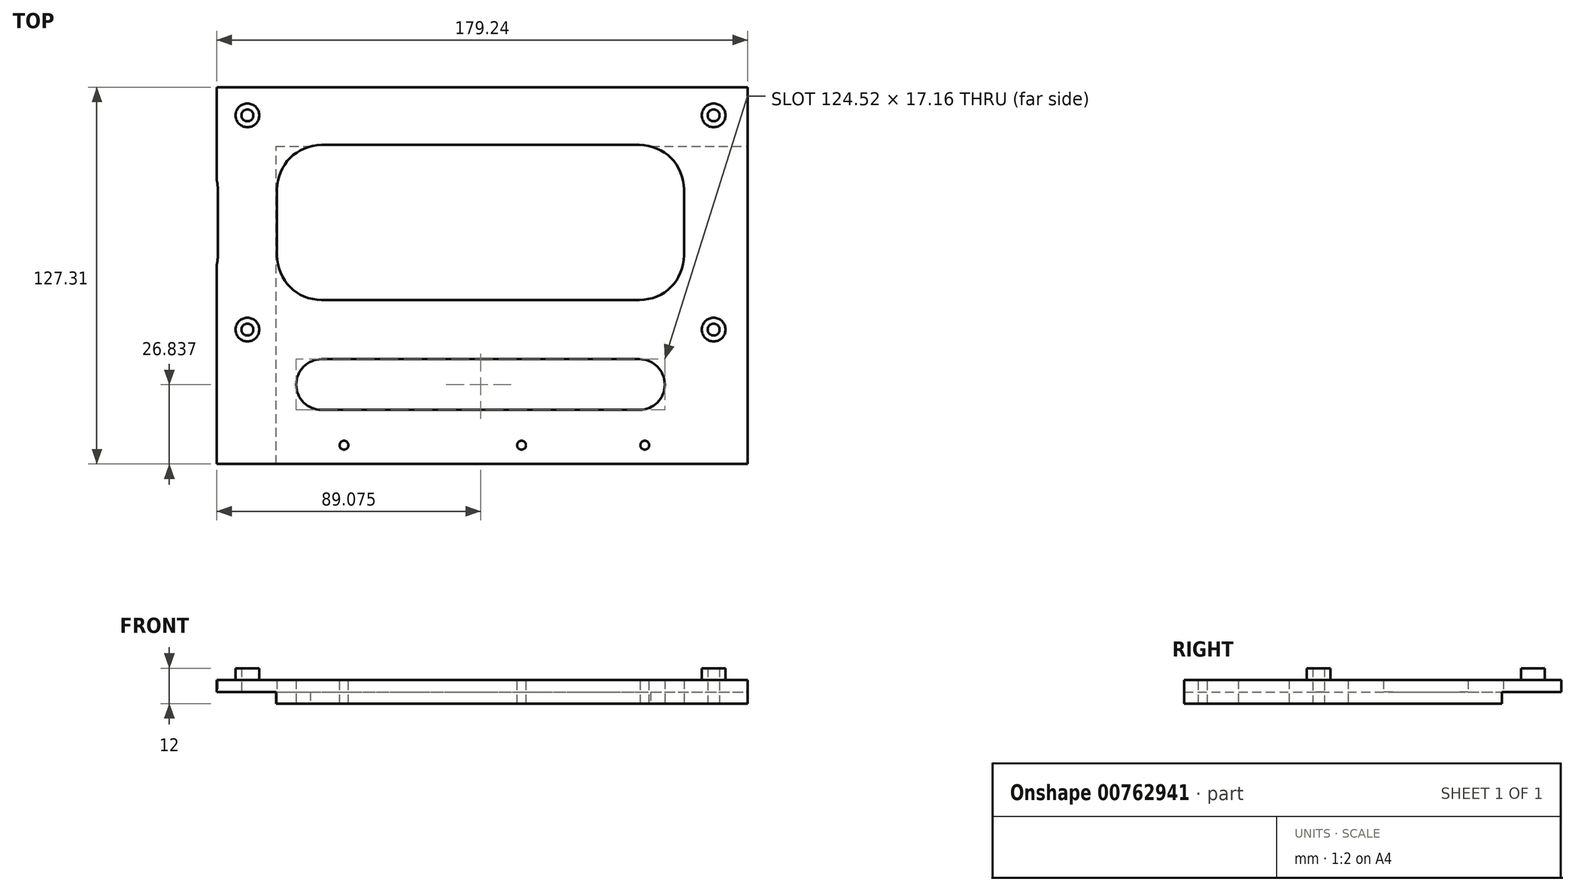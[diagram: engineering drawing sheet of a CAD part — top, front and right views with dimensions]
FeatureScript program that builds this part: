
annotation { "Feature Type Name" : "Feature", "Feature Type Description" : "" }
export const myFeature = defineFeature(function(context is Context, id is Id, definition is map)
    precondition{}
    {
        {
            var Q0;
            Q0=qCreatedBy(makeId("Top.planeOp"),FACE);
            var sketch = newSketch(context, id + "F0", { "sketchPlane" : qUnion([Q0])});
            skLineSegment(sketch, "E0.bottom", {"start": v(-84.85, 211.43) * mm, "end": v(248.95, 211.43) * mm});
            skLineSegment(sketch, "E0.left", {"start": v(-84.85, 211.43) * mm, "end": v(-84.85, -69.57) * mm});
            skLineSegment(sketch, "E0.right", {"start": v(248.95, 211.43) * mm, "end": v(248.95, -32.4) * mm});
            skCircle(sketch, "E1", {"center": v(-44.42, 203.18) * mm, "radius": 2 * mm});
            skCircle(sketch, "E2", {"center": v(-44.42, 48.24) * mm, "radius": 2 * mm});
            skCircle(sketch, "E3", {"center": v(-44.42, -24.15) * mm, "radius": 2 * mm});
            skCircle(sketch, "E4", {"center": v(80.04, -24.15) * mm, "radius": 2 * mm});
            skCircle(sketch, "E5", {"center": v(80.04, 48.24) * mm, "radius": 2 * mm});
            skCircle(sketch, "E6", {"center": v(80.04, 203.18) * mm, "radius": 2 * mm});
            skCircle(sketch, "E7", {"center": v(237.52, 48.24) * mm, "radius": 2 * mm});
            skCircle(sketch, "E8", {"center": v(237.52, -24.15) * mm, "radius": 2 * mm});
            skCircle(sketch, "E9", {"center": v(237.52, 180.32) * mm, "radius": 2 * mm});
            skLineSegment(sketch, "E10.left", {"start": v(-34.42, 178.12) * mm, "end": v(-34.42, 73.3) * mm});
            skLineSegment(sketch, "E10.right", {"start": v(70.04, 178.12) * mm, "end": v(70.04, 73.3) * mm});
            skLineSegment(sketch, "E11.bottom", {"start": v(-19.36, 58.24) * mm, "end": v(54.99, 58.24) * mm});
            skLineSegment(sketch, "E11.top", {"start": v(-19.36, 38.24) * mm, "end": v(54.99, 38.24) * mm});
            skLineSegment(sketch, "E12.left", {"start": v(-34.42, 23.18) * mm, "end": v(-34.42, 0.9) * mm});
            skLineSegment(sketch, "E12.right", {"start": v(70.04, 23.18) * mm, "end": v(70.04, 0.9) * mm});
            skLineSegment(sketch, "E13.left", {"start": v(90.04, 23.18) * mm, "end": v(90.04, 0.9) * mm});
            skLineSegment(sketch, "E13.right", {"start": v(227.52, 23.18) * mm, "end": v(227.52, 0.9) * mm});
            skLineSegment(sketch, "E14.bottom", {"start": v(212.47, -14.15) * mm, "end": v(105.1, -14.15) * mm});
            skLineSegment(sketch, "E14.top", {"start": v(212.47, 38.24) * mm, "end": v(105.1, 38.24) * mm});
            skLineSegment(sketch, "E15.bottom", {"start": v(212.47, 58.24) * mm, "end": v(105.1, 58.24) * mm});
            skLineSegment(sketch, "E15.top", {"start": v(212.47, 193.18) * mm, "end": v(105.1, 193.18) * mm});
            skLineSegment(sketch, "E16.left", {"start": v(90.04, 178.12) * mm, "end": v(90.04, 73.3) * mm});
            skLineSegment(sketch, "E17", {"start": v(-19.36, -14.15) * mm, "end": v(54.99, -14.15) * mm});
            skLineSegment(sketch, "E18", {"start": v(-19.36, 193.18) * mm, "end": v(54.99, 193.18) * mm});
            skLineSegment(sketch, "E19", {"start": v(212.47, 170.32) * mm, "end": v(212.47, 193.18) * mm});
            skLineSegment(sketch, "E20", {"start": v(227.52, 155.26) * mm, "end": v(227.52, 73.3) * mm});
            skLineSegment(sketch, "E21", {"start": v(54.99, -34.15) * mm, "end": v(-19.36, -34.15) * mm});
            skLineSegment(sketch, "E22.MirrorCS", {"start": v(212.47, -51.31) * mm, "end": v(105.1, -51.31) * mm});
            skLineSegment(sketch, "E23.MirrorCS", {"start": v(212.47, -34.15) * mm, "end": v(105.1, -34.15) * mm});
            skLineSegment(sketch, "E24.MirrorCS", {"start": v(-19.36, -51.31) * mm, "end": v(54.99, -51.31) * mm});
            skLineSegment(sketch, "E25", {"start": v(-84.85, -69.57) * mm, "end": v(248.95, -69.57) * mm});
            skLineSegment(sketch, "E26", {"start": v(248.95, -32.4) * mm, "end": v(248.95, -69.57) * mm});
            skLineSegment(sketch, "E27", {"start": v(-54.42, -42.73) * mm, "end": v(-54.42, 33.18) * mm});
            skLineSegment(sketch, "E28", {"start": v(-66.28, 33.18) * mm, "end": v(-66.28, -42.73) * mm});
            skArc(sketch, "E29", {"start": v(-54.42, 33.18) * mm, "mid": v(-60.35, 39.1) * mm, "end": v(-66.28, 33.18) * mm});
            skArc(sketch, "E30", {"start": v(-66.28, -42.73) * mm, "mid": v(-60.35, -48.66) * mm, "end": v(-54.42, -42.73) * mm});
            skArc(sketch, "E31", {"start": v(-34.42, 0.9) * mm, "mid": v(-30, -9.74) * mm, "end": v(-19.36, -14.15) * mm});
            skArc(sketch, "E32", {"start": v(-19.36, 38.24) * mm, "mid": v(-30, 33.83) * mm, "end": v(-34.42, 23.18) * mm});
            skArc(sketch, "E33", {"start": v(70.04, 23.18) * mm, "mid": v(65.63, 33.83) * mm, "end": v(54.99, 38.24) * mm});
            skArc(sketch, "E34", {"start": v(54.99, -14.15) * mm, "mid": v(65.63, -9.74) * mm, "end": v(70.04, 0.9) * mm});
            skArc(sketch, "E35", {"start": v(-19.36, -34.15) * mm, "mid": v(-27.94, -42.73) * mm, "end": v(-19.36, -51.31) * mm});
            skArc(sketch, "E36", {"start": v(54.99, -51.31) * mm, "mid": v(63.56, -42.73) * mm, "end": v(54.99, -34.15) * mm});
            skArc(sketch, "E37", {"start": v(105.1, -34.15) * mm, "mid": v(96.52, -42.73) * mm, "end": v(105.1, -51.31) * mm});
            skArc(sketch, "E38", {"start": v(212.47, -51.31) * mm, "mid": v(221.04, -42.73) * mm, "end": v(212.47, -34.15) * mm});
            skArc(sketch, "E39", {"start": v(212.47, -14.15) * mm, "mid": v(223.11, -9.74) * mm, "end": v(227.52, 0.9) * mm});
            skArc(sketch, "E40", {"start": v(227.52, 23.18) * mm, "mid": v(223.11, 33.83) * mm, "end": v(212.47, 38.24) * mm});
            skArc(sketch, "E41", {"start": v(105.1, 38.24) * mm, "mid": v(94.46, 33.83) * mm, "end": v(90.04, 23.18) * mm});
            skArc(sketch, "E42", {"start": v(90.04, 0.9) * mm, "mid": v(94.46, -9.74) * mm, "end": v(105.1, -14.15) * mm});
            skArc(sketch, "E43", {"start": v(105.1, 193.18) * mm, "mid": v(94.46, 188.77) * mm, "end": v(90.04, 178.12) * mm});
            skArc(sketch, "E44", {"start": v(70.04, 178.12) * mm, "mid": v(65.63, 188.77) * mm, "end": v(54.99, 193.18) * mm});
            skArc(sketch, "E45", {"start": v(-19.36, 193.18) * mm, "mid": v(-30, 188.77) * mm, "end": v(-34.42, 178.12) * mm});
            skArc(sketch, "E46", {"start": v(-34.42, 73.3) * mm, "mid": v(-30, 62.65) * mm, "end": v(-19.36, 58.24) * mm});
            skArc(sketch, "E47", {"start": v(54.99, 58.24) * mm, "mid": v(65.63, 62.65) * mm, "end": v(70.04, 73.3) * mm});
            skArc(sketch, "E48", {"start": v(90.04, 73.3) * mm, "mid": v(94.46, 62.65) * mm, "end": v(105.1, 58.24) * mm});
            skArc(sketch, "E49", {"start": v(212.47, 58.24) * mm, "mid": v(223.11, 62.65) * mm, "end": v(227.52, 73.3) * mm});
            skArc(sketch, "E50", {"start": v(227.52, 155.26) * mm, "mid": v(223.11, 165.9) * mm, "end": v(212.47, 170.32) * mm});
            skArc(sketch, "E51.MirrorCS", {"start": v(-54.42, 63.3) * mm, "mid": v(-60.35, 57.36) * mm, "end": v(-66.28, 63.3) * mm});
            skLineSegment(sketch, "E52.MirrorCS", {"start": v(-66.28, 63.3) * mm, "end": v(-66.28, 180.32) * mm});
            skLineSegment(sketch, "E53.MirrorCS", {"start": v(-54.42, 180.32) * mm, "end": v(-54.42, 63.3) * mm});
            skArc(sketch, "E54.MirrorCS", {"start": v(-66.28, 180.32) * mm, "mid": v(-60.35, 186.25) * mm, "end": v(-54.42, 180.32) * mm});
            skSolve(sketch);
        }
        {
            var Q0;
            Q0=makeQuery(id+"F0.imprint","IMPRINT",FACE,{"disambiguationData":[TD([[makeQuery(id+"F0.imprint","IMPRINT",EDGE,{"derivedFrom":sQuery(id+"F0.wireOp",EDGE,"E0.bottom")}),-1.0]])]});
            extrude(context, id + "F1", {"entities" : qUnion([Q0]), "depth" : 8 * mm, "offsetDistance" : 25 * mm});
        }
        {
            var Q0;
            Q0=makeQuery(id+"F1.opExtrude","CAP_FACE",FACE,{"disambiguationData":[OSD([sQuery(id+"F0.wireOp",EDGE,"E0.bottom"),sQuery(id+"F0.wireOp",EDGE,"E0.left"),sQuery(id+"F0.wireOp",EDGE,"E0.right"),sQuery(id+"F0.wireOp",EDGE,"E1"),sQuery(id+"F0.wireOp",EDGE,"E2"),sQuery(id+"F0.wireOp",EDGE,"E3"),sQuery(id+"F0.wireOp",EDGE,"E4"),sQuery(id+"F0.wireOp",EDGE,"E5"),sQuery(id+"F0.wireOp",EDGE,"E6"),sQuery(id+"F0.wireOp",EDGE,"E7"),sQuery(id+"F0.wireOp",EDGE,"E8"),sQuery(id+"F0.wireOp",EDGE,"E9"),sQuery(id+"F0.wireOp",EDGE,"E10.left"),sQuery(id+"F0.wireOp",EDGE,"E10.right"),sQuery(id+"F0.wireOp",EDGE,"E11.bottom"),sQuery(id+"F0.wireOp",EDGE,"E11.top"),sQuery(id+"F0.wireOp",EDGE,"E12.left"),sQuery(id+"F0.wireOp",EDGE,"E12.right"),sQuery(id+"F0.wireOp",EDGE,"E13.left"),sQuery(id+"F0.wireOp",EDGE,"E13.right"),sQuery(id+"F0.wireOp",EDGE,"E14.bottom"),sQuery(id+"F0.wireOp",EDGE,"E14.top"),sQuery(id+"F0.wireOp",EDGE,"E15.bottom"),sQuery(id+"F0.wireOp",EDGE,"E15.top"),sQuery(id+"F0.wireOp",EDGE,"E16.left"),sQuery(id+"F0.wireOp",EDGE,"E17"),sQuery(id+"F0.wireOp",EDGE,"E18"),sQuery(id+"F0.wireOp",EDGE,"E19"),sQuery(id+"F0.wireOp",EDGE,"E20"),sQuery(id+"F0.wireOp",EDGE,"E21"),sQuery(id+"F0.wireOp",EDGE,"E22.MirrorCS"),sQuery(id+"F0.wireOp",EDGE,"E23.MirrorCS"),sQuery(id+"F0.wireOp",EDGE,"E24.MirrorCS"),sQuery(id+"F0.wireOp",EDGE,"E25"),sQuery(id+"F0.wireOp",EDGE,"E26"),sQuery(id+"F0.wireOp",EDGE,"E27"),sQuery(id+"F0.wireOp",EDGE,"E28"),sQuery(id+"F0.wireOp",EDGE,"E29"),sQuery(id+"F0.wireOp",EDGE,"E30"),sQuery(id+"F0.wireOp",EDGE,"E31"),sQuery(id+"F0.wireOp",EDGE,"E32"),sQuery(id+"F0.wireOp",EDGE,"E33"),sQuery(id+"F0.wireOp",EDGE,"E34"),sQuery(id+"F0.wireOp",EDGE,"E35"),sQuery(id+"F0.wireOp",EDGE,"E36"),sQuery(id+"F0.wireOp",EDGE,"E37"),sQuery(id+"F0.wireOp",EDGE,"E38"),sQuery(id+"F0.wireOp",EDGE,"E39"),sQuery(id+"F0.wireOp",EDGE,"E40"),sQuery(id+"F0.wireOp",EDGE,"E41"),sQuery(id+"F0.wireOp",EDGE,"E42"),sQuery(id+"F0.wireOp",EDGE,"E43"),sQuery(id+"F0.wireOp",EDGE,"E44"),sQuery(id+"F0.wireOp",EDGE,"E45"),sQuery(id+"F0.wireOp",EDGE,"E46"),sQuery(id+"F0.wireOp",EDGE,"E47"),sQuery(id+"F0.wireOp",EDGE,"E48"),sQuery(id+"F0.wireOp",EDGE,"E49"),sQuery(id+"F0.wireOp",EDGE,"E50"),sQuery(id+"F0.wireOp",EDGE,"E51.MirrorCS"),sQuery(id+"F0.wireOp",EDGE,"E52.MirrorCS"),sQuery(id+"F0.wireOp",EDGE,"E53.MirrorCS"),sQuery(id+"F0.wireOp",EDGE,"E54.MirrorCS")])],"isStart":false});
            var sketch = newSketch(context, id + "F2", { "sketchPlane" : qUnion([Q0])});
            skLineSegment(sketch, "E55.bottom", {"start": v(-84.85, 211.43) * mm, "end": v(15.15, 211.43) * mm});
            skLineSegment(sketch, "E55.top", {"start": v(-84.85, 71.43) * mm, "end": v(-81.85, 71.43) * mm});
            skLineSegment(sketch, "E55.left", {"start": v(-84.85, 211.43) * mm, "end": v(-84.85, 71.43) * mm});
            skLineSegment(sketch, "E55.right", {"start": v(15.15, 211.43) * mm, "end": v(15.15, 208.43) * mm});
            skLineSegment(sketch, "E56", {"start": v(-81.85, 208.43) * mm, "end": v(-81.85, 71.43) * mm});
            skLineSegment(sketch, "E57", {"start": v(-81.85, 208.43) * mm, "end": v(15.15, 208.43) * mm});
            skSolve(sketch);
        }
        {
            var Q0;
            Q0=makeQuery(id+"F2.imprint","IMPRINT",FACE,{"disambiguationData":[TD([[makeQuery(id+"F2.imprint","IMPRINT",EDGE,{"derivedFrom":sQuery(id+"F2.wireOp",EDGE,"E55.bottom")}),-1.0]])]});
            extrude(context, id + "F3", {"entities" : qUnion([Q0]), "operationType" : NewBodyOperationType.ADD, "depth" : 185 * mm, "offsetDistance" : 25 * mm});
        }
        {
            var Q0;
            Q0=makeQuery(id+"F3.boolean.opBoolean","MERGE",FACE,{"derivedFrom":[makeQuery(id+"F1.opExtrude","SWEPT_FACE",FACE,{"disambiguationData":[OSD([sQuery(id+"F0.wireOp",EDGE,"E0.left")])]}),makeQuery(id+"F3.opExtrude","SWEPT_FACE",FACE,{"disambiguationData":[OSD([sQuery(id+"F2.wireOp",EDGE,"E55.left")])]})]});
            var sketch = newSketch(context, id + "F4", { "sketchPlane" : qUnion([Q0])});
            skLineSegment(sketch, "E58", {"start": v(-211.43, 193) * mm, "end": v(-206.43, 193) * mm});
            skLineSegment(sketch, "E59", {"start": v(-206.43, 193) * mm, "end": v(-158.54, 40) * mm});
            skLineSegment(sketch, "E60.1", {"start": v(-201.43, 143.55) * mm, "end": v(-169.02, 40) * mm});
            skLineSegment(sketch, "E61.trimOffspring", {"start": v(-201.43, 143.55) * mm, "end": v(-201.43, 40) * mm});
            skLineSegment(sketch, "E62", {"start": v(-211.43, 0) * mm, "end": v(-211.43, 58.72) * mm});
            skLineSegment(sketch, "E63", {"start": v(-60.87, 0) * mm, "end": v(-60.87, 40) * mm});
            skLineSegment(sketch, "E64", {"start": v(-60.87, 40) * mm, "end": v(-158.54, 40) * mm});
            skPoint(sketch, "E65.orphan", {"position": v(-211.43, 40) * mm});
            skLineSegment(sketch, "E66.trimOffspring", {"start": v(-169.02, 40) * mm, "end": v(-201.43, 40) * mm});
            skLineSegment(sketch, "E67", {"start": v(-60.87, 0) * mm, "end": v(-211.43, 0) * mm});
            skSolve(sketch);
        }
        {
            var Q0;
            Q0=makeQuery(id+"F4.imprint","IMPRINT",FACE,{"disambiguationData":[TD([[makeQuery(id+"F4.imprint","IMPRINT",EDGE,{"derivedFrom":sQuery(id+"F4.wireOp",EDGE,"E60.1")}),-1.0]])]});
            var Q1;
            {var subQ0=sQuery(id+"F4.wireOp",EDGE,"E59");Q1=makeQuery(id+"F4.imprint","IMPRINT",FACE,{"disambiguationData":[TD([[makeQuery(id+"F4.imprint","IMPRINT",EDGE,{"derivedFrom":subQ0}),1.0]])]});}
            extrude(context, id + "F5", {"entities" : qUnion([Q0, Q1]), "operationType" : NewBodyOperationType.REMOVE, "oppositeDirection" : true, "depth" : 5 * mm, "offsetDistance" : 25 * mm});
        }
        {
            var Q0;
            Q0=makeQuery(id+"F3.boolean.opBoolean","MERGE",FACE,{"derivedFrom":[makeQuery(id+"F1.opExtrude","SWEPT_FACE",FACE,{"disambiguationData":[OSD([sQuery(id+"F0.wireOp",EDGE,"E0.bottom")])]}),makeQuery(id+"F3.opExtrude","SWEPT_FACE",FACE,{"disambiguationData":[OSD([sQuery(id+"F2.wireOp",EDGE,"E55.bottom")])]})]});
            var sketch = newSketch(context, id + "F6", { "sketchPlane" : qUnion([Q0])});
            skLineSegment(sketch, "E68", {"start": v(81.85, 181.6) * mm, "end": v(81.85, 188.15) * mm});
            skCircle(sketch, "E69", {"center": v(75.35, 185.63) * mm, "radius": 2.5 * mm});
            skCircle(sketch, "E70", {"center": v(75.35, 161.63) * mm, "radius": 2.5 * mm});
            skCircle(sketch, "E71", {"center": v(75.35, 47.63) * mm, "radius": 2.5 * mm});
            skCircle(sketch, "E72", {"center": v(65.35, 47.63) * mm, "radius": 2.5 * mm});
            skCircle(sketch, "E73", {"center": v(1.35, 47.63) * mm, "radius": 2.5 * mm});
            skCircle(sketch, "E74", {"center": v(1.35, 71.63) * mm, "radius": 2.5 * mm});
            skCircle(sketch, "E75", {"center": v(1.35, 185.63) * mm, "radius": 2.5 * mm});
            skCircle(sketch, "E76", {"center": v(11.35, 185.63) * mm, "radius": 2.5 * mm});
            skLineSegment(sketch, "E77.left", {"start": v(12.85, 55.13) * mm, "end": v(12.85, 83.03) * mm});
            skLineSegment(sketch, "E77.right", {"start": v(67.85, 148.13) * mm, "end": v(67.85, 178.13) * mm});
            skLineSegment(sketch, "E78", {"start": v(75.35, 148.13) * mm, "end": v(67.85, 148.13) * mm});
            skLineSegment(sketch, "E79", {"start": v(12.85, 55.13) * mm, "end": v(75.35, 55.13) * mm});
            skLineSegment(sketch, "E80", {"start": v(2.85, 178.13) * mm, "end": v(67.85, 178.13) * mm});
            skLineSegment(sketch, "E81", {"start": v(75.35, 55.13) * mm, "end": v(75.35, 148.13) * mm});
            skLineSegment(sketch, "E82", {"start": v(2.85, 178.13) * mm, "end": v(1.35, 83.22) * mm});
            skLineSegment(sketch, "E83", {"start": v(1.35, 83.22) * mm, "end": v(12.85, 83.03) * mm});
            skSolve(sketch);
        }
        {
            var Q0;
            Q0=makeQuery(id+"F6.imprint","IMPRINT",FACE,{"disambiguationData":[TD([[makeQuery(id+"F6.imprint","IMPRINT",EDGE,{"derivedFrom":sQuery(id+"F6.wireOp",EDGE,"E77.left")}),-1.0]])]});
            var Q1;
            Q1=makeQuery(id+"F6.imprint","IMPRINT",FACE,{"disambiguationData":[TD([[makeQuery(id+"F6.imprint","IMPRINT",EDGE,{"derivedFrom":sQuery(id+"F6.wireOp",EDGE,"E76")}),1.0]])]});
            var Q2;
            Q2=makeQuery(id+"F6.imprint","IMPRINT",FACE,{"disambiguationData":[TD([[makeQuery(id+"F6.imprint","IMPRINT",EDGE,{"derivedFrom":sQuery(id+"F6.wireOp",EDGE,"E75")}),1.0]])]});
            var Q3;
            Q3=makeQuery(id+"F6.imprint","IMPRINT",FACE,{"disambiguationData":[TD([[makeQuery(id+"F6.imprint","IMPRINT",EDGE,{"derivedFrom":sQuery(id+"F6.wireOp",EDGE,"E70")}),1.0]])]});
            var Q4;
            Q4=makeQuery(id+"F6.imprint","IMPRINT",FACE,{"disambiguationData":[TD([[makeQuery(id+"F6.imprint","IMPRINT",EDGE,{"derivedFrom":sQuery(id+"F6.wireOp",EDGE,"E69")}),1.0]])]});
            var Q5;
            Q5=makeQuery(id+"F6.imprint","IMPRINT",FACE,{"disambiguationData":[TD([[makeQuery(id+"F6.imprint","IMPRINT",EDGE,{"derivedFrom":sQuery(id+"F6.wireOp",EDGE,"E71")}),1.0]])]});
            var Q6;
            Q6=makeQuery(id+"F6.imprint","IMPRINT",FACE,{"disambiguationData":[TD([[makeQuery(id+"F6.imprint","IMPRINT",EDGE,{"derivedFrom":sQuery(id+"F6.wireOp",EDGE,"E72")}),1.0]])]});
            var Q7;
            Q7=makeQuery(id+"F6.imprint","IMPRINT",FACE,{"disambiguationData":[TD([[makeQuery(id+"F6.imprint","IMPRINT",EDGE,{"derivedFrom":sQuery(id+"F6.wireOp",EDGE,"E73")}),1.0]])]});
            var Q8;
            Q8=makeQuery(id+"F6.imprint","IMPRINT",FACE,{"disambiguationData":[TD([[makeQuery(id+"F6.imprint","IMPRINT",EDGE,{"derivedFrom":sQuery(id+"F6.wireOp",EDGE,"E74")}),1.0]])]});
            extrude(context, id + "F7", {"entities" : qUnion([Q0, Q1, Q2, Q3, Q4, Q5, Q6, Q7, Q8]), "operationType" : NewBodyOperationType.REMOVE, "oppositeDirection" : true, "depth" : 5 * mm, "offsetDistance" : 25 * mm});
        }
        {
            var Q0;
            Q0=makeQuery(id+"F5.boolean.opBoolean","COPY",FACE,{"derivedFrom":makeQuery(id+"F5.opExtrude","SWEPT_FACE",FACE,{"disambiguationData":[OSD([sQuery(id+"F4.wireOp",EDGE,"E66.trimOffspring")])]})});
            var sketch = newSketch(context, id + "F8", { "sketchPlane" : qUnion([Q0])});
            skLineSegment(sketch, "E84.bottom", {"start": v(-81.85, 208.49) * mm, "end": v(14.15, 208.49) * mm});
            skLineSegment(sketch, "E84.left", {"start": v(-81.85, 208.49) * mm, "end": v(-81.85, 71.52) * mm});
            skPoint(sketch, "E85.orphan", {"position": v(-81.85, 80.66) * mm});
            skLineSegment(sketch, "E86", {"start": v(-81.85, 71.52) * mm, "end": v(14.15, 208.49) * mm});
            skLineSegment(sketch, "E87.0", {"start": v(-71.85, 198.49) * mm, "end": v(-5.07, 198.49) * mm});
            skLineSegment(sketch, "E87.1", {"start": v(-71.85, 198.49) * mm, "end": v(-71.85, 103.21) * mm});
            skLineSegment(sketch, "E87.2", {"start": v(-71.85, 103.21) * mm, "end": v(-5.07, 198.49) * mm});
            skPoint(sketch, "E88.endSnap0", {"position": v(-44.4, 203.14) * mm});
            skCircle(sketch, "E89", {"center": v(-44.4, 203.14) * mm, "radius": 2.01 * mm});
            skSolve(sketch);
        }
        {
            var Q0;
            {var subQ5=sQuery(id+"F8.wireOp",EDGE,"E84.bottom");Q0=makeQuery(id+"F8.imprint","IMPRINT",FACE,{"disambiguationData":[TD([[makeQuery(id+"F8.imprint","IMPRINT",EDGE,{"derivedFrom":subQ5}),-1.0]])]});}
            extrude(context, id + "F9", {"entities" : qUnion([Q0]), "operationType" : NewBodyOperationType.ADD, "depth" : -3 * mm, "offsetDistance" : 25 * mm});
        }
        {
            var Q0;
            Q0=makeQuery(id+"F1.opExtrude","CAP_FACE",FACE,{"disambiguationData":[OSD([sQuery(id+"F0.wireOp",EDGE,"E0.bottom"),sQuery(id+"F0.wireOp",EDGE,"E0.left"),sQuery(id+"F0.wireOp",EDGE,"E0.right"),sQuery(id+"F0.wireOp",EDGE,"E1"),sQuery(id+"F0.wireOp",EDGE,"E2"),sQuery(id+"F0.wireOp",EDGE,"E3"),sQuery(id+"F0.wireOp",EDGE,"E4"),sQuery(id+"F0.wireOp",EDGE,"E5"),sQuery(id+"F0.wireOp",EDGE,"E6"),sQuery(id+"F0.wireOp",EDGE,"E7"),sQuery(id+"F0.wireOp",EDGE,"E8"),sQuery(id+"F0.wireOp",EDGE,"E9"),sQuery(id+"F0.wireOp",EDGE,"E10.left"),sQuery(id+"F0.wireOp",EDGE,"E10.right"),sQuery(id+"F0.wireOp",EDGE,"E11.bottom"),sQuery(id+"F0.wireOp",EDGE,"E11.top"),sQuery(id+"F0.wireOp",EDGE,"E12.left"),sQuery(id+"F0.wireOp",EDGE,"E12.right"),sQuery(id+"F0.wireOp",EDGE,"E13.left"),sQuery(id+"F0.wireOp",EDGE,"E13.right"),sQuery(id+"F0.wireOp",EDGE,"E14.bottom"),sQuery(id+"F0.wireOp",EDGE,"E14.top"),sQuery(id+"F0.wireOp",EDGE,"E15.bottom"),sQuery(id+"F0.wireOp",EDGE,"E15.top"),sQuery(id+"F0.wireOp",EDGE,"E16.left"),sQuery(id+"F0.wireOp",EDGE,"E17"),sQuery(id+"F0.wireOp",EDGE,"E18"),sQuery(id+"F0.wireOp",EDGE,"E19"),sQuery(id+"F0.wireOp",EDGE,"E20"),sQuery(id+"F0.wireOp",EDGE,"E21"),sQuery(id+"F0.wireOp",EDGE,"E22.MirrorCS"),sQuery(id+"F0.wireOp",EDGE,"E23.MirrorCS"),sQuery(id+"F0.wireOp",EDGE,"E24.MirrorCS"),sQuery(id+"F0.wireOp",EDGE,"E25"),sQuery(id+"F0.wireOp",EDGE,"E26"),sQuery(id+"F0.wireOp",EDGE,"E27"),sQuery(id+"F0.wireOp",EDGE,"E28"),sQuery(id+"F0.wireOp",EDGE,"E29"),sQuery(id+"F0.wireOp",EDGE,"E30"),sQuery(id+"F0.wireOp",EDGE,"E31"),sQuery(id+"F0.wireOp",EDGE,"E32"),sQuery(id+"F0.wireOp",EDGE,"E33"),sQuery(id+"F0.wireOp",EDGE,"E34"),sQuery(id+"F0.wireOp",EDGE,"E35"),sQuery(id+"F0.wireOp",EDGE,"E36"),sQuery(id+"F0.wireOp",EDGE,"E37"),sQuery(id+"F0.wireOp",EDGE,"E38"),sQuery(id+"F0.wireOp",EDGE,"E39"),sQuery(id+"F0.wireOp",EDGE,"E40"),sQuery(id+"F0.wireOp",EDGE,"E41"),sQuery(id+"F0.wireOp",EDGE,"E42"),sQuery(id+"F0.wireOp",EDGE,"E43"),sQuery(id+"F0.wireOp",EDGE,"E44"),sQuery(id+"F0.wireOp",EDGE,"E45"),sQuery(id+"F0.wireOp",EDGE,"E46"),sQuery(id+"F0.wireOp",EDGE,"E47"),sQuery(id+"F0.wireOp",EDGE,"E48"),sQuery(id+"F0.wireOp",EDGE,"E49"),sQuery(id+"F0.wireOp",EDGE,"E50"),sQuery(id+"F0.wireOp",EDGE,"E51.MirrorCS"),sQuery(id+"F0.wireOp",EDGE,"E52.MirrorCS"),sQuery(id+"F0.wireOp",EDGE,"E53.MirrorCS"),sQuery(id+"F0.wireOp",EDGE,"E54.MirrorCS")])],"isStart":false});
            var sketch = newSketch(context, id + "F10", { "sketchPlane" : qUnion([Q0])});
            skCircle(sketch, "E90", {"center": v(80.04, 203.18) * mm, "radius": 2 * mm});
            skCircle(sketch, "E91.0", {"center": v(80.04, 203.18) * mm, "radius": 4 * mm});
            skLineSegment(sketch, "E92.0", {"start": v(243.95, -64.57) * mm, "end": v(243.95, 206.43) * mm});
            skLineSegment(sketch, "E92.1", {"start": v(-79.85, -64.57) * mm, "end": v(243.95, -64.57) * mm});
            skLineSegment(sketch, "E92.2", {"start": v(243.95, 206.43) * mm, "end": v(20.15, 206.43) * mm});
            skLineSegment(sketch, "E92.3", {"start": v(-79.85, 66.43) * mm, "end": v(-79.85, -64.57) * mm});
            skLineSegment(sketch, "E92.4", {"start": v(20.15, 206.43) * mm, "end": v(20.15, 203.43) * mm});
            skLineSegment(sketch, "E92.5", {"start": v(20.15, 203.43) * mm, "end": v(-76.85, 203.43) * mm});
            skLineSegment(sketch, "E92.6", {"start": v(-76.85, 203.43) * mm, "end": v(-76.85, 66.43) * mm});
            skLineSegment(sketch, "E92.7", {"start": v(-76.85, 66.43) * mm, "end": v(-79.85, 66.43) * mm});
            skCircle(sketch, "E93.0", {"center": v(237.52, 180.32) * mm, "radius": 4 * mm});
            skCircle(sketch, "E94.0", {"center": v(237.52, 48.24) * mm, "radius": 4 * mm});
            skCircle(sketch, "E95.0", {"center": v(80.04, 48.24) * mm, "radius": 4 * mm});
            skCircle(sketch, "E96.0", {"center": v(237.52, -24.15) * mm, "radius": 4 * mm});
            skCircle(sketch, "E97.0", {"center": v(80.04, -24.15) * mm, "radius": 4 * mm});
            skCircle(sketch, "E98.0", {"center": v(-44.42, -24.15) * mm, "radius": 4 * mm});
            skCircle(sketch, "E99.0", {"center": v(-44.42, 48.24) * mm, "radius": 4 * mm});
            skCircle(sketch, "E100.0", {"center": v(-44.42, 203.18) * mm, "radius": 4 * mm});
            skSolve(sketch);
        }
        {
            var Q0;
            Q0=makeQuery(id+"F10.imprint","IMPRINT",FACE,{"disambiguationData":[TD([[makeQuery(id+"F10.imprint","IMPRINT",EDGE,{"derivedFrom":sQuery(id+"F10.wireOp",EDGE,"E94.0")}),1.0]])]});
            var Q1;
            Q1=makeQuery(id+"F10.imprint","IMPRINT",FACE,{"disambiguationData":[TD([[makeQuery(id+"F10.imprint","IMPRINT",EDGE,{"derivedFrom":sQuery(id+"F10.wireOp",EDGE,"E96.0")}),1.0]])]});
            var Q2;
            Q2=makeQuery(id+"F10.imprint","IMPRINT",FACE,{"disambiguationData":[TD([[makeQuery(id+"F10.imprint","IMPRINT",EDGE,{"derivedFrom":sQuery(id+"F10.wireOp",EDGE,"E95.0")}),1.0]])]});
            var Q3;
            Q3=makeQuery(id+"F10.imprint","IMPRINT",FACE,{"disambiguationData":[TD([[makeQuery(id+"F10.imprint","IMPRINT",EDGE,{"derivedFrom":sQuery(id+"F10.wireOp",EDGE,"E97.0")}),1.0]])]});
            extrude(context, id + "F11", {"entities" : qUnion([Q0, Q1, Q2, Q3]), "operationType" : NewBodyOperationType.ADD, "depth" : 4 * mm, "offsetDistance" : 25 * mm});
        }
        {
            var Q0;
            Q0=makeQuery(id+"F1.opExtrude","SWEPT_FACE",FACE,{"disambiguationData":[OSD([sQuery(id+"F0.wireOp",EDGE,"E0.right"),sQuery(id+"F0.wireOp",EDGE,"E26")])]});
            var sketch = newSketch(context, id + "F12", { "sketchPlane" : qUnion([Q0])});
            skLineSegment(sketch, "E101.left", {"start": v(37.74, 4) * mm, "end": v(37.74, 0) * mm});
            skLineSegment(sketch, "E101.right", {"start": v(57.74, 8) * mm, "end": v(57.74, 4) * mm});
            skLineSegment(sketch, "E102", {"start": v(37.74, 4) * mm, "end": v(57.74, 4) * mm});
            skSolve(sketch);
        }
        {
            var Q0;
            {var subQ3=sQuery(id+"F12.wireOp",EDGE,"E101.left");Q0=makeQuery(id+"F12.imprint","IMPRINT",FACE,{"disambiguationData":[TD([[makeQuery(id+"F12.imprint","IMPRINT",EDGE,{"derivedFrom":subQ3}),1.0]])]});}
            extrude(context, id + "F13", {"entities" : qUnion([Q0]), "operationType" : NewBodyOperationType.REMOVE, "oppositeDirection" : true, "depth" : 340 * mm, "offsetDistance" : 25 * mm});
        }
        {
            var Q0;
            Q0=makeQuery(id+"F3.boolean.opBoolean","MERGE",FACE,{"derivedFrom":[makeQuery(id+"F1.opExtrude","SWEPT_FACE",FACE,{"disambiguationData":[OSD([sQuery(id+"F0.wireOp",EDGE,"E0.bottom")])]}),makeQuery(id+"F3.opExtrude","SWEPT_FACE",FACE,{"disambiguationData":[OSD([sQuery(id+"F2.wireOp",EDGE,"E55.bottom")])]})]});
            var sketch = newSketch(context, id + "F14", { "sketchPlane" : qUnion([Q0])});
            skLineSegment(sketch, "E103.left", {"start": v(-69.71, 4) * mm, "end": v(-69.71, 8) * mm});
            skLineSegment(sketch, "E103.right", {"start": v(-89.71, 0) * mm, "end": v(-89.71, 4) * mm});
            skLineSegment(sketch, "E104", {"start": v(-89.71, 4) * mm, "end": v(-69.71, 4) * mm});
            skLineSegment(sketch, "E105", {"start": v(-89.71, 0) * mm, "end": v(93.97, 0) * mm});
            skLineSegment(sketch, "E106", {"start": v(93.97, 0) * mm, "end": v(93.97, 17.64) * mm});
            skLineSegment(sketch, "E107", {"start": v(-20.75, 10.88) * mm, "end": v(-69.71, 8) * mm});
            skLineSegment(sketch, "E108.bottom", {"start": v(93.97, 0) * mm, "end": v(-20.75, 0) * mm});
            skLineSegment(sketch, "E108.top", {"start": v(93.97, 194.9) * mm, "end": v(-20.75, 194.9) * mm});
            skLineSegment(sketch, "E108.left", {"start": v(93.97, 0) * mm, "end": v(93.97, 194.9) * mm});
            skLineSegment(sketch, "E108.right", {"start": v(-20.75, 10.88) * mm, "end": v(-20.75, 194.9) * mm});
            skSolve(sketch);
        }
        {
            var Q0;
            Q0=qSketchRegion(id+"F14",true);
            var Q1;
            {var subQ4=sQuery(id+"F14.wireOp",EDGE,"E103.left");Q1=makeQuery(id+"F14.imprint","IMPRINT",FACE,{"disambiguationData":[TD([[makeQuery(id+"F14.imprint","IMPRINT",EDGE,{"derivedFrom":subQ4}),-1.0]])]});}
            extrude(context, id + "F15", {"entities" : qUnion([Q0, Q1]), "operationType" : NewBodyOperationType.REMOVE, "oppositeDirection" : true, "depth" : 320 * mm, "offsetDistance" : 25 * mm});
        }
        {
            var Q0;
            Q0=makeQuery(id+"F1.opExtrude","CAP_FACE",FACE,{"disambiguationData":[OSD([sQuery(id+"F0.wireOp",EDGE,"E0.bottom"),sQuery(id+"F0.wireOp",EDGE,"E0.left"),sQuery(id+"F0.wireOp",EDGE,"E0.right"),sQuery(id+"F0.wireOp",EDGE,"E1"),sQuery(id+"F0.wireOp",EDGE,"E2"),sQuery(id+"F0.wireOp",EDGE,"E3"),sQuery(id+"F0.wireOp",EDGE,"E4"),sQuery(id+"F0.wireOp",EDGE,"E5"),sQuery(id+"F0.wireOp",EDGE,"E6"),sQuery(id+"F0.wireOp",EDGE,"E7"),sQuery(id+"F0.wireOp",EDGE,"E8"),sQuery(id+"F0.wireOp",EDGE,"E9"),sQuery(id+"F0.wireOp",EDGE,"E10.left"),sQuery(id+"F0.wireOp",EDGE,"E10.right"),sQuery(id+"F0.wireOp",EDGE,"E11.bottom"),sQuery(id+"F0.wireOp",EDGE,"E11.top"),sQuery(id+"F0.wireOp",EDGE,"E12.left"),sQuery(id+"F0.wireOp",EDGE,"E12.right"),sQuery(id+"F0.wireOp",EDGE,"E13.left"),sQuery(id+"F0.wireOp",EDGE,"E13.right"),sQuery(id+"F0.wireOp",EDGE,"E14.bottom"),sQuery(id+"F0.wireOp",EDGE,"E14.top"),sQuery(id+"F0.wireOp",EDGE,"E15.bottom"),sQuery(id+"F0.wireOp",EDGE,"E15.top"),sQuery(id+"F0.wireOp",EDGE,"E16.left"),sQuery(id+"F0.wireOp",EDGE,"E17"),sQuery(id+"F0.wireOp",EDGE,"E18"),sQuery(id+"F0.wireOp",EDGE,"E19"),sQuery(id+"F0.wireOp",EDGE,"E20"),sQuery(id+"F0.wireOp",EDGE,"E21"),sQuery(id+"F0.wireOp",EDGE,"E22.MirrorCS"),sQuery(id+"F0.wireOp",EDGE,"E23.MirrorCS"),sQuery(id+"F0.wireOp",EDGE,"E24.MirrorCS"),sQuery(id+"F0.wireOp",EDGE,"E25"),sQuery(id+"F0.wireOp",EDGE,"E26"),sQuery(id+"F0.wireOp",EDGE,"E27"),sQuery(id+"F0.wireOp",EDGE,"E28"),sQuery(id+"F0.wireOp",EDGE,"E29"),sQuery(id+"F0.wireOp",EDGE,"E30"),sQuery(id+"F0.wireOp",EDGE,"E31"),sQuery(id+"F0.wireOp",EDGE,"E32"),sQuery(id+"F0.wireOp",EDGE,"E33"),sQuery(id+"F0.wireOp",EDGE,"E34"),sQuery(id+"F0.wireOp",EDGE,"E35"),sQuery(id+"F0.wireOp",EDGE,"E36"),sQuery(id+"F0.wireOp",EDGE,"E37"),sQuery(id+"F0.wireOp",EDGE,"E38"),sQuery(id+"F0.wireOp",EDGE,"E39"),sQuery(id+"F0.wireOp",EDGE,"E40"),sQuery(id+"F0.wireOp",EDGE,"E41"),sQuery(id+"F0.wireOp",EDGE,"E42"),sQuery(id+"F0.wireOp",EDGE,"E43"),sQuery(id+"F0.wireOp",EDGE,"E44"),sQuery(id+"F0.wireOp",EDGE,"E45"),sQuery(id+"F0.wireOp",EDGE,"E46"),sQuery(id+"F0.wireOp",EDGE,"E47"),sQuery(id+"F0.wireOp",EDGE,"E48"),sQuery(id+"F0.wireOp",EDGE,"E49"),sQuery(id+"F0.wireOp",EDGE,"E50"),sQuery(id+"F0.wireOp",EDGE,"E51.MirrorCS"),sQuery(id+"F0.wireOp",EDGE,"E52.MirrorCS"),sQuery(id+"F0.wireOp",EDGE,"E53.MirrorCS"),sQuery(id+"F0.wireOp",EDGE,"E54.MirrorCS")])],"isStart":false});
            var sketch = newSketch(context, id + "F16", { "sketchPlane" : qUnion([Q0])});
            skCircle(sketch, "E109", {"center": v(214.26, -63.22) * mm, "radius": 1.5 * mm});
            skPoint(sketch, "E109.centerSnap0", {"position": v(212.47, -63.22) * mm});
            skCircle(sketch, "E110", {"center": v(112.66, -63.22) * mm, "radius": 1.5 * mm});
            skCircle(sketch, "E111", {"center": v(172.65, -63.22) * mm, "radius": 1.5 * mm});
            skSolve(sketch);
        }
        {
            var Q0;
            Q0 = qSketchRegion(id + "F16", true);
            extrude(context, id + "F17", {"entities" : qUnion([Q0]), "operationType" : NewBodyOperationType.REMOVE, "oppositeDirection" : true, "depth" : 25 * mm, "offsetDistance" : 25 * mm});
        }
    });
